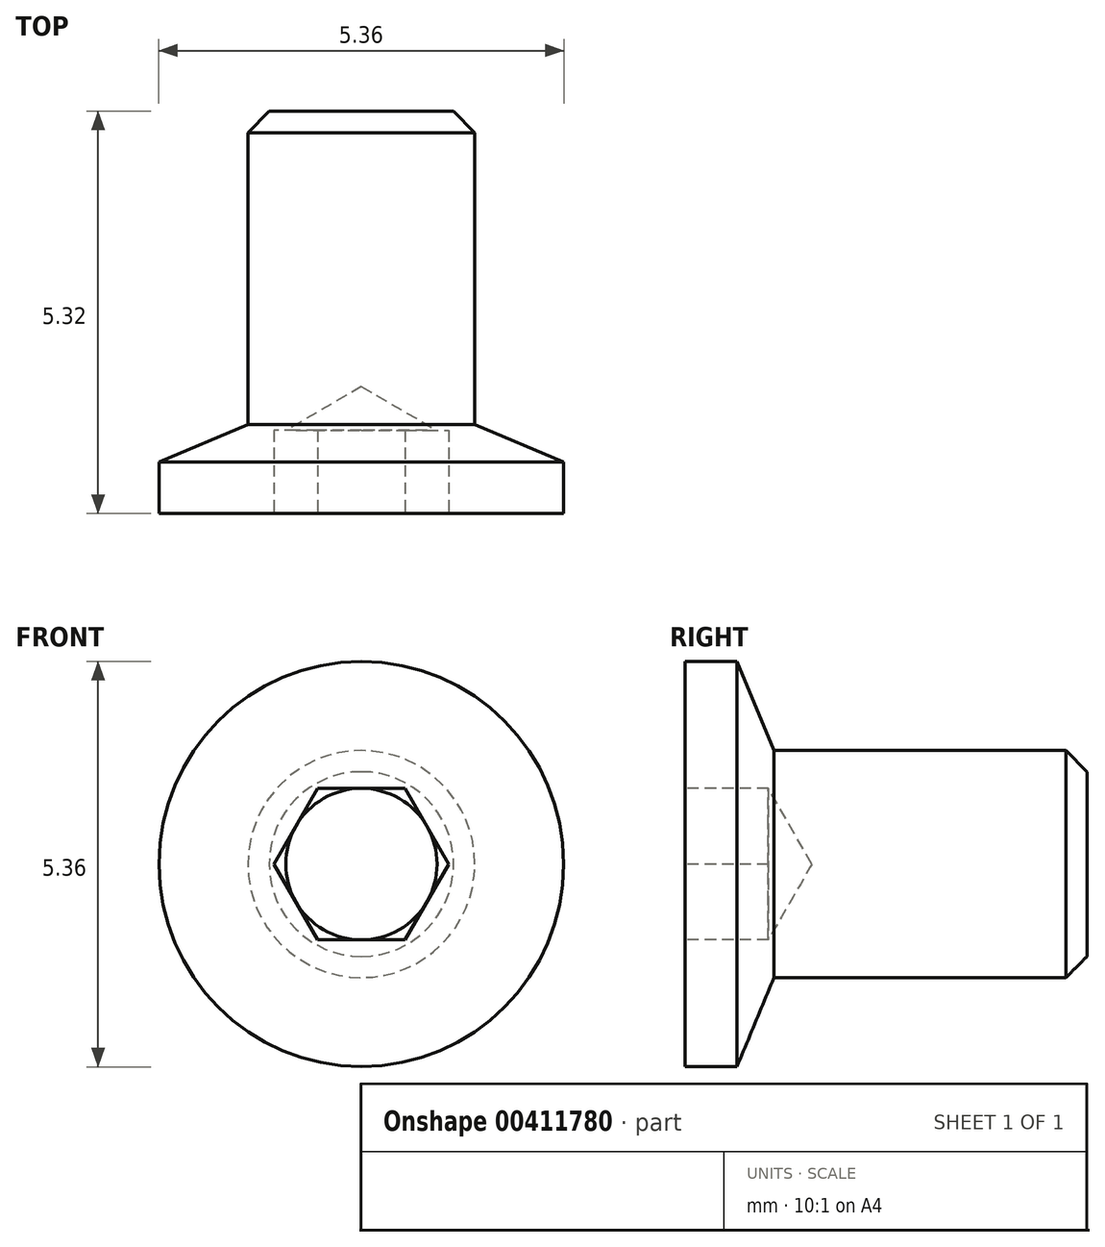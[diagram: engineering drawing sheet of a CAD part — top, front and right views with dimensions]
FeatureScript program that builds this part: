
annotation { "Feature Type Name" : "Feature", "Feature Type Description" : "" }
export const myFeature = defineFeature(function(context is Context, id is Id, definition is map)
    precondition{}
    {
        {
            var Q0;
            Q0=qCreatedBy(makeId("Front.planeOp"),FACE);
            var sketch = newSketch(context, id + "F0", { "sketchPlane" : qUnion([Q0])});
            skCircle(sketch, "E0", {"center": v(0, 0) * mm, "radius": 2.68 * mm});
            skCircle(sketch, "E1.cCircle", {"center": v(0, 0) * mm, "radius": 1 * mm, "construction": true});
            skLineSegment(sketch, "E1.0", {"start": v(-0.58, 1) * mm, "end": v(0.58, 1) * mm});
            skLineSegment(sketch, "E1.1", {"start": v(0.58, 1) * mm, "end": v(1.15, 0) * mm});
            skLineSegment(sketch, "E1.2", {"start": v(1.15, 0) * mm, "end": v(0.58, -1) * mm});
            skLineSegment(sketch, "E1.3", {"start": v(0.58, -1) * mm, "end": v(-0.58, -1) * mm});
            skLineSegment(sketch, "E1.4", {"start": v(-0.58, -1) * mm, "end": v(-1.15, 0) * mm});
            skLineSegment(sketch, "E1.5", {"start": v(-1.15, 0) * mm, "end": v(-0.58, 1) * mm});
            skPoint(sketch, "E1.0.midPoint", {"position": v(0, 1) * mm});
            skSolve(sketch);
        }
        {
            var Q0;
            Q0=qSketchRegion(id+"F0",true);
            var Q1;
            Q1=makeQuery(id+"F0.imprint","IMPRINT",FACE,{"disambiguationData":[TD([[makeQuery(id+"F0.imprint","IMPRINT",EDGE,{"derivedFrom":sQuery(id+"F0.wireOp",EDGE,"E1.0")}),-1.0]])]});
            extrude(context, id + "F1", {"entities" : qUnion([Q0, Q1]), "oppositeDirection" : true, "depth" : 0.69 * mm});
        }
        {
            var Q0;
            Q0=makeQuery(id+"F0.imprint","IMPRINT",FACE,{"disambiguationData":[TD([[makeQuery(id+"F0.imprint","IMPRINT",EDGE,{"derivedFrom":sQuery(id+"F0.wireOp",EDGE,"E0")}),1.0]])]});
            cPlane(context, id + "F2", {"entities" : qUnion([Q0]), "cplaneType" : CPlaneType.OFFSET, "offset" : 1.18 * mm, "oppositeDirection" : true, "width" : 150 * mm, "height" : 150 * mm});
        }
        {
            var Q0;
            Q0=qCreatedBy(id+"F2.planeOp",FACE);
            var sketch = newSketch(context, id + "F3", { "sketchPlane" : qUnion([Q0])});
            skPoint(sketch, "E2.0", {"position": v(0, 0) * mm});
            skCircle(sketch, "E3", {"center": v(0, 0) * mm, "radius": 1.5 * mm});
            skSolve(sketch);
        }
        {
            var Q1;
            Q1=makeQuery(id+"F1.opExtrude","CAP_FACE",FACE,{"disambiguationData":[OSD([sQuery(id+"F0.wireOp",EDGE,"E0")])],"isStart":false});
            var Q2;
            Q2=makeQuery(id+"F3.imprint","IMPRINT",FACE,{"disambiguationData":[TD([[makeQuery(id+"F3.imprint","IMPRINT",EDGE,{"derivedFrom":sQuery(id+"F3.wireOp",EDGE,"E3")}),1.0]])]});
            loft(context, id + "F4", {"operationType" : NewBodyOperationType.ADD, "sheetProfilesArray" : [{ "sheetProfileEntities" : qUnion([Q1]) }, { "sheetProfileEntities" : qUnion([Q2]) }]});
        }
        {
            var Q0;
            Q0=makeQuery(id+"F4.opLoft","CAP_FACE",FACE,{"disambiguationData":[OSD([makeQuery(id+"F3.imprint","IMPRINT",FACE,{"disambiguationData":[TD([[makeQuery(id+"F3.imprint","IMPRINT",EDGE,{"derivedFrom":sQuery(id+"F3.wireOp",EDGE,"E3")}),1.0]])]})])],"isStart":true});
            extrude(context, id + "F5", {"entities" : qUnion([Q0]), "operationType" : NewBodyOperationType.ADD, "depth" : (4.14 - 0.28) * mm});
        }
        {
            var Q0;
            Q0=makeQuery(id+"F5.opExtrude","CAP_FACE",FACE,{"disambiguationData":[OSD([makeQuery(id+"F3.imprint","IMPRINT",FACE,{"disambiguationData":[TD([[makeQuery(id+"F3.imprint","IMPRINT",EDGE,{"derivedFrom":sQuery(id+"F3.wireOp",EDGE,"E3")}),1.0]])]})])],"isStart":false});
            cPlane(context, id + "F6", {"entities" : qUnion([Q0]), "cplaneType" : CPlaneType.OFFSET, "offset" : 0.28 * mm, "width" : 150 * mm, "height" : 150 * mm});
        }
        {
            var Q0;
            Q0=qCreatedBy(id+"F6.planeOp",FACE);
            var sketch = newSketch(context, id + "F7", { "sketchPlane" : qUnion([Q0])});
            skPoint(sketch, "E4.0", {"position": v(0, 0) * mm});
            skCircle(sketch, "E5", {"center": v(0, 0) * mm, "radius": 1.22 * mm});
            skSolve(sketch);
        }
        {
            var Q1;
            Q1=makeQuery(id+"F7.imprint","IMPRINT",FACE,{"disambiguationData":[TD([[makeQuery(id+"F7.imprint","IMPRINT",EDGE,{"derivedFrom":sQuery(id+"F7.wireOp",EDGE,"E5")}),1.0]])]});
            var Q2;
            Q2=makeQuery(id+"F5.opExtrude","CAP_FACE",FACE,{"disambiguationData":[OSD([makeQuery(id+"F3.imprint","IMPRINT",FACE,{"disambiguationData":[TD([[makeQuery(id+"F3.imprint","IMPRINT",EDGE,{"derivedFrom":sQuery(id+"F3.wireOp",EDGE,"E3")}),1.0]])]})])],"isStart":false});
            loft(context, id + "F8", {"operationType" : NewBodyOperationType.ADD, "sheetProfilesArray" : [{ "sheetProfileEntities" : qUnion([Q1]) }, { "sheetProfileEntities" : qUnion([Q2]) }]});
        }
        {
            var Q0;
            Q0=makeQuery(id+"F0.imprint","IMPRINT",FACE,{"disambiguationData":[TD([[makeQuery(id+"F0.imprint","IMPRINT",EDGE,{"derivedFrom":sQuery(id+"F0.wireOp",EDGE,"E1.0")}),-1.0]])]});
            extrude(context, id + "F9", {"entities" : qUnion([Q0]), "operationType" : NewBodyOperationType.REMOVE, "oppositeDirection" : true, "depth" : 1.1 * mm});
        }
        {
            var Q0;
            Q0=makeQuery(id+"F0.imprint","IMPRINT",FACE,{"disambiguationData":[TD([[makeQuery(id+"F0.imprint","IMPRINT",EDGE,{"derivedFrom":sQuery(id+"F0.wireOp",EDGE,"E0")}),1.0]])]});
            cPlane(context, id + "F10", {"entities" : qUnion([Q0]), "cplaneType" : CPlaneType.OFFSET, "offset" : 1.1 * mm, "oppositeDirection" : true, "width" : 150 * mm, "height" : 150 * mm});
        }
        {
            var Q0;
            Q0=qCreatedBy(id+"F10.planeOp",FACE);
            var sketch = newSketch(context, id + "F11", { "sketchPlane" : qUnion([Q0])});
            skPoint(sketch, "E6.0", {"position": v(0, 0) * mm});
            skCircle(sketch, "E7", {"center": v(0, 0) * mm, "radius": 1 * mm});
            skSolve(sketch);
        }
        {
            var Q0;
            Q0=qCreatedBy(id+"F10.planeOp",FACE);
            cPlane(context, id + "F12", {"entities" : qUnion([Q0]), "cplaneType" : CPlaneType.OFFSET, "offset" : 0.58 * mm, "oppositeDirection" : true, "width" : 150 * mm, "height" : 150 * mm});
        }
        {
            var Q0;
            Q0=qCreatedBy(id+"F12.planeOp",FACE);
            var sketch = newSketch(context, id + "F13", { "sketchPlane" : qUnion([Q0])});
            skPoint(sketch, "E8.0", {"position": v(0, 0) * mm});
            skSolve(sketch);
        }
        {
            var Q1;
            Q1=makeQuery(id+"F11.imprint","IMPRINT",FACE,{"disambiguationData":[TD([[makeQuery(id+"F11.imprint","IMPRINT",EDGE,{"derivedFrom":sQuery(id+"F11.wireOp",EDGE,"E7")}),1.0]])]});
            var Q2;
            Q2=sQuery(id+"F13.wireOp",VERTEX,"E8.0");
            loft(context, id + "F14", {"operationType" : NewBodyOperationType.REMOVE, "sheetProfilesArray" : [{ "sheetProfileEntities" : qUnion([Q1]) }, { "sheetProfileEntities" : qUnion([Q2]) }]});
        }
    });
